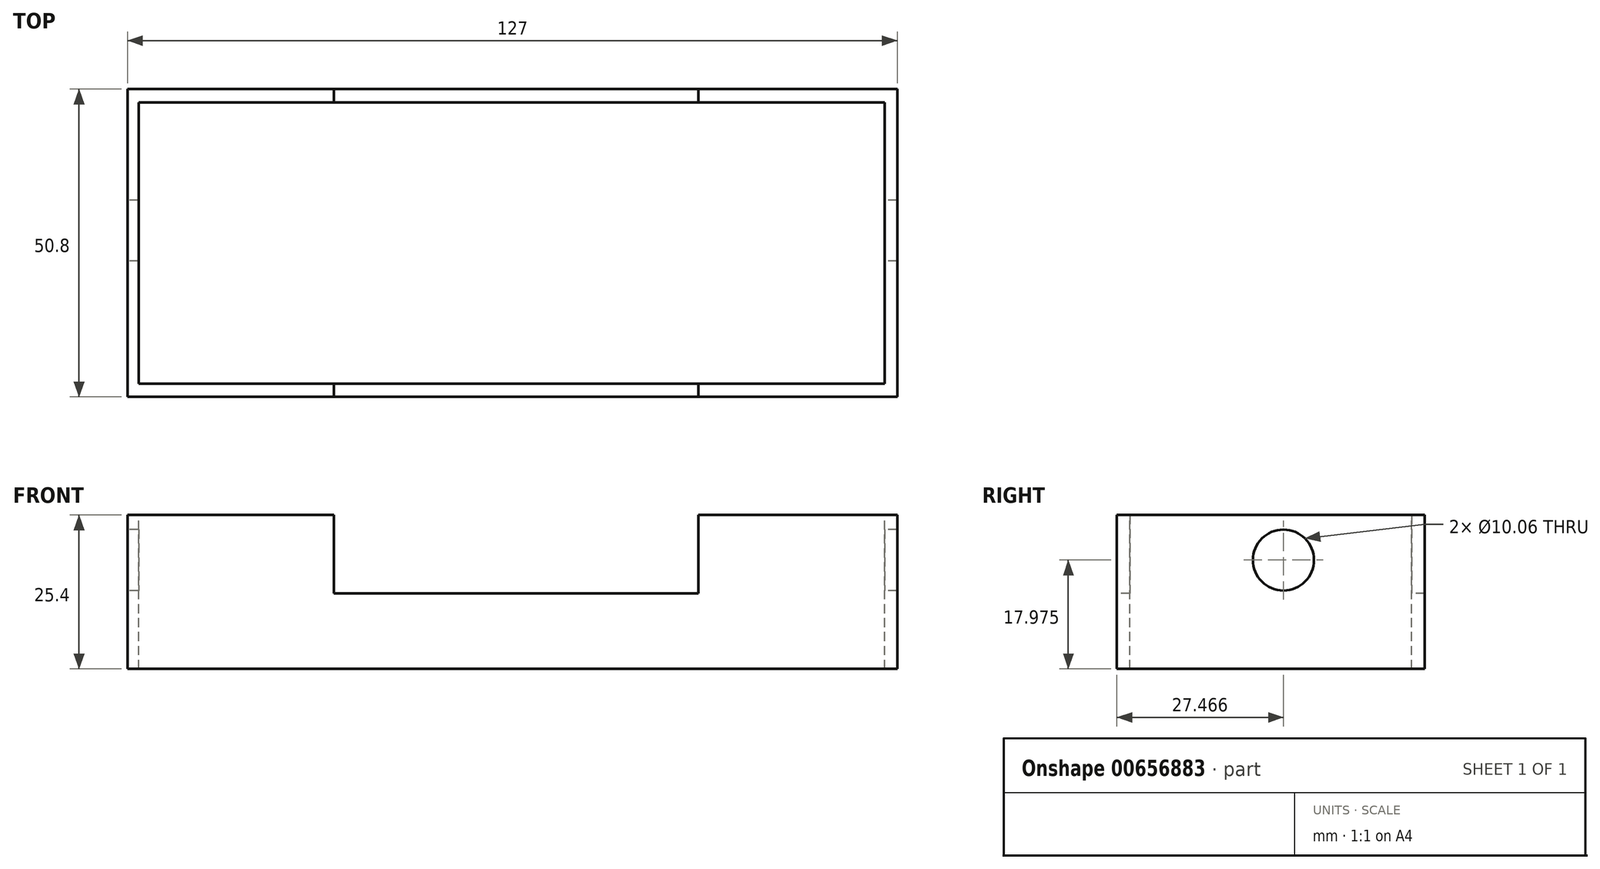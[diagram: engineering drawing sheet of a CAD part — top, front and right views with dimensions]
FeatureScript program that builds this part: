
annotation { "Feature Type Name" : "Feature", "Feature Type Description" : "" }
export const myFeature = defineFeature(function(context is Context, id is Id, definition is map)
    precondition{}
    {
        {
            var Q0;
            Q0=qCreatedBy(makeId("Top.planeOp"),FACE);
            var sketch = newSketch(context, id + "F0", { "sketchPlane" : qUnion([Q0])});
            skLineSegment(sketch, "E0.bottom", {"start": v(-63.67, 9.6) * mm, "end": v(63.33, 9.6) * mm});
            skLineSegment(sketch, "E0.top", {"start": v(-63.67, -41.2) * mm, "end": v(63.33, -41.2) * mm});
            skLineSegment(sketch, "E0.left", {"start": v(-63.67, 9.6) * mm, "end": v(-63.67, -41.2) * mm});
            skLineSegment(sketch, "E0.right", {"start": v(63.33, 9.6) * mm, "end": v(63.33, -41.2) * mm});
            skSolve(sketch);
        }
        {
            var Q0;
            Q0=makeQuery(id+"F0.imprint","IMPRINT",FACE,{"disambiguationData":[TD([[makeQuery(id+"F0.imprint","IMPRINT",EDGE,{"derivedFrom":sQuery(id+"F0.wireOp",EDGE,"E0.bottom")}),-1.0]])]});
            extrude(context, id + "F1", {"entities" : qUnion([Q0]), "depth" : 25.4 * mm, "offsetDistance" : 25.4 * mm});
        }
        {
            var Q0;
            Q0=makeQuery(id+"F1.opExtrude","CAP_FACE",FACE,{"disambiguationData":[OSD([sQuery(id+"F0.wireOp",EDGE,"E0.bottom"),sQuery(id+"F0.wireOp",EDGE,"E0.top"),sQuery(id+"F0.wireOp",EDGE,"E0.left"),sQuery(id+"F0.wireOp",EDGE,"E0.right")])],"isStart":false});
            var sketch = newSketch(context, id + "F2", { "sketchPlane" : qUnion([Q0])});
            skLineSegment(sketch, "E1.bottom", {"start": v(-61.8, 7.4) * mm, "end": v(61.24, 7.4) * mm});
            skLineSegment(sketch, "E1.top", {"start": v(-61.8, -39.04) * mm, "end": v(61.24, -39.04) * mm});
            skLineSegment(sketch, "E1.left", {"start": v(-61.8, 7.4) * mm, "end": v(-61.8, -39.04) * mm});
            skLineSegment(sketch, "E1.right", {"start": v(61.24, 7.4) * mm, "end": v(61.24, -39.04) * mm});
            skSolve(sketch);
        }
        {
            var Q0;
            Q0=qSketchRegion(id+"F2",true);
            extrude(context, id + "F3", {"entities" : qUnion([Q0]), "operationType" : NewBodyOperationType.REMOVE, "oppositeDirection" : true, "depth" : 44.45 * mm, "offsetDistance" : 25.4 * mm});
        }
        {
            var Q0;
            Q0=makeQuery(id+"F1.opExtrude","SWEPT_FACE",FACE,{"disambiguationData":[OSD([sQuery(id+"F0.wireOp",EDGE,"E0.left")])]});
            var sketch = newSketch(context, id + "F4", { "sketchPlane" : qUnion([Q0])});
            skCircle(sketch, "E2", {"center": v(13.73, 17.97) * mm, "radius": 5.03 * mm});
            skSolve(sketch);
        }
        {
            var Q0;
            Q0=makeQuery(id+"F4.imprint","IMPRINT",FACE,{"disambiguationData":[TD([[makeQuery(id+"F4.imprint","IMPRINT",EDGE,{"derivedFrom":sQuery(id+"F4.wireOp",EDGE,"E2")}),1.0]])]});
            extrude(context, id + "F5", {"entities" : qUnion([Q0]), "operationType" : NewBodyOperationType.REMOVE, "oppositeDirection" : true, "depth" : 156.46 * mm, "offsetDistance" : 25.4 * mm});
        }
        {
            var Q0;
            Q0=makeQuery(id+"F1.opExtrude","SWEPT_FACE",FACE,{"disambiguationData":[OSD([sQuery(id+"F0.wireOp",EDGE,"E0.top")])]});
            var sketch = newSketch(context, id + "F6", { "sketchPlane" : qUnion([Q0])});
            skLineSegment(sketch, "E3.bottom", {"start": v(-29.59, 34.38) * mm, "end": v(30.51, 34.38) * mm});
            skLineSegment(sketch, "E3.top", {"start": v(-29.59, 12.44) * mm, "end": v(30.51, 12.44) * mm});
            skLineSegment(sketch, "E3.left", {"start": v(-29.59, 34.38) * mm, "end": v(-29.59, 12.44) * mm});
            skLineSegment(sketch, "E3.right", {"start": v(30.51, 34.38) * mm, "end": v(30.51, 12.44) * mm});
            skSolve(sketch);
        }
        {
            var Q0;
            {var subQ0=sQuery(id+"F6.wireOp",EDGE,"E3.top");Q0=makeQuery(id+"F6.imprint","IMPRINT",FACE,{"disambiguationData":[TD([[makeQuery(id+"F6.imprint","IMPRINT",EDGE,{"derivedFrom":subQ0}),1.0]])]});}
            extrude(context, id + "F7", {"entities" : qUnion([Q0]), "operationType" : NewBodyOperationType.REMOVE, "oppositeDirection" : true, "depth" : 78.23 * mm, "offsetDistance" : 25.4 * mm});
        }
    });
